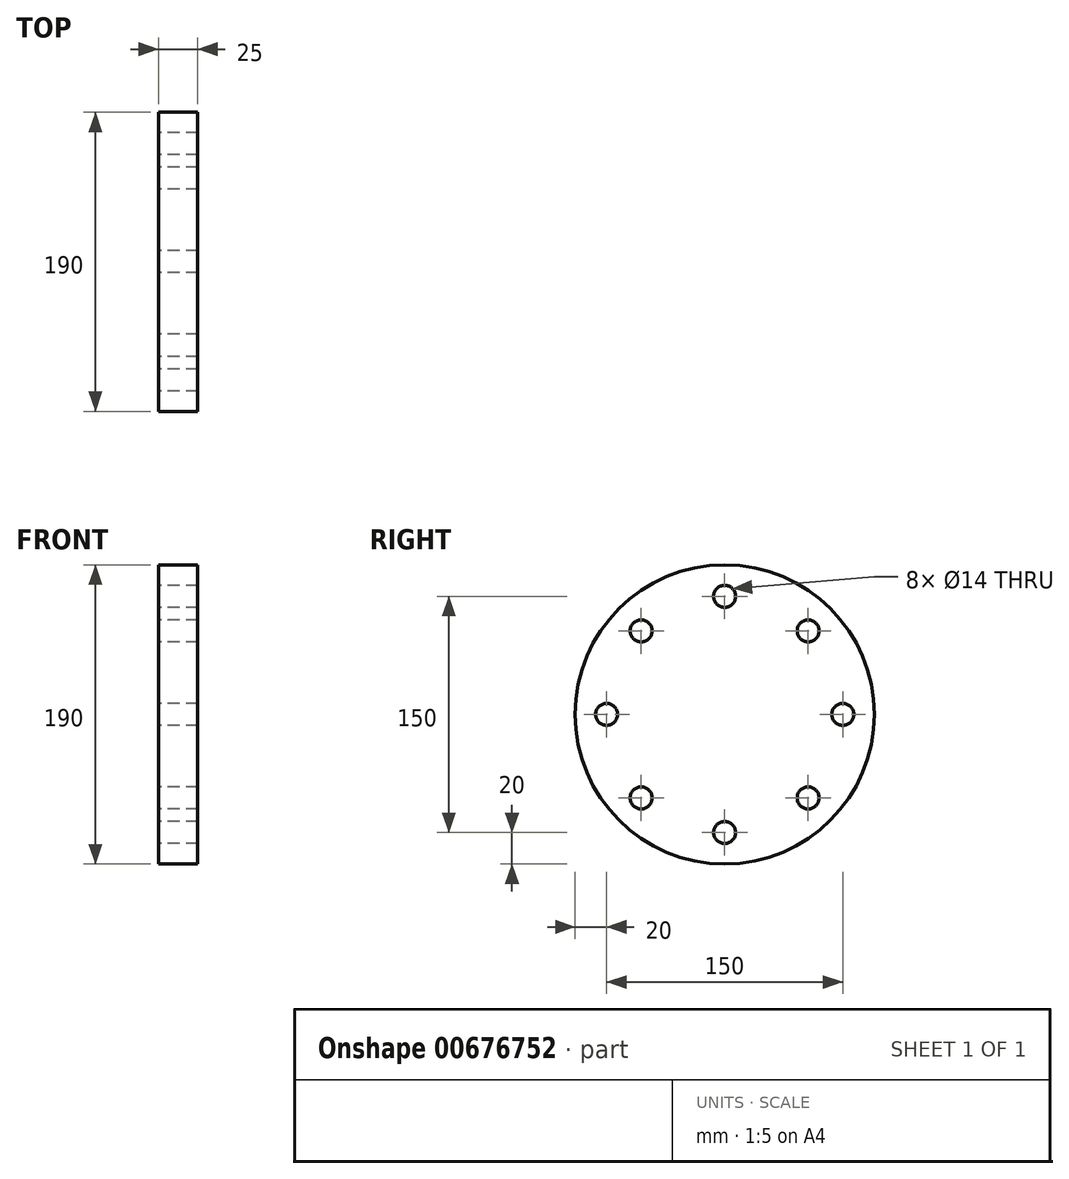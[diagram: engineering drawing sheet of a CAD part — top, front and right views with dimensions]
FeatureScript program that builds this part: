
annotation { "Feature Type Name" : "Feature", "Feature Type Description" : "" }
export const myFeature = defineFeature(function(context is Context, id is Id, definition is map)
    precondition{}
    {
        {
            var Q0;
            Q0=qCreatedBy(makeId("Right.planeOp"),FACE);
            var sketch = newSketch(context, id + "F0", { "sketchPlane" : qUnion([Q0])});
            skCircle(sketch, "E0", {"center": v(0, 0) * mm, "radius": 95 * mm});
            skCircle(sketch, "E1", {"center": v(0, 0) * mm, "radius": 75 * mm});
            skCircle(sketch, "E2", {"center": v(0, 75) * mm, "radius": 7 * mm});
            skCircle(sketch, "E3.1.0", {"center": v(-53.03, 53.03) * mm, "radius": 7 * mm});
            skCircle(sketch, "E3.2.0", {"center": v(-75, 0) * mm, "radius": 7 * mm});
            skCircle(sketch, "E3.3.0", {"center": v(-53.03, -53.03) * mm, "radius": 7 * mm});
            skCircle(sketch, "E3.4.0", {"center": v(0, -75) * mm, "radius": 7 * mm});
            skCircle(sketch, "E3.5.0", {"center": v(53.03, -53.03) * mm, "radius": 7 * mm});
            skCircle(sketch, "E3.6.0", {"center": v(75, 0) * mm, "radius": 7 * mm});
            skCircle(sketch, "E3.7.0", {"center": v(53.03, 53.03) * mm, "radius": 7 * mm});
            skSolve(sketch);
        }
        {
            var Q0;
            Q0=makeQuery(id+"F0.imprint","IMPRINT",FACE,{"disambiguationData":[TD([[makeQuery(id+"F0.imprint","IMPRINT",EDGE,{"derivedFrom":sQuery(id+"F0.wireOp",EDGE,"E0")}),1.0]])]});
            var Q1;
            {var subQ1=sQuery(id+"F0.wireOp",EDGE,"E1");var subQ20=sQuery(id+"F0.wireOp",EDGE,"E3.7.0");var subQ21=makeQuery(id+"F0.imprint","INTERSECT",VERTEX,{"disambiguationData":[OD(0.0)],"derivedFrom":[subQ1,subQ20]});Q1=makeQuery(id+"F0.imprint","IMPRINT",FACE,{"disambiguationData":[TD([[makeQuery(id+"F0.imprint","IMPRINT",EDGE,{"disambiguationData":[TD([[subQ21,1.0]])],"derivedFrom":subQ1}),1.0]])]});}
            extrude(context, id + "F1", {"entities" : qUnion([Q0, Q1]), "depth" : 25 * mm, "offsetDistance" : 25 * mm});
        }
    });
